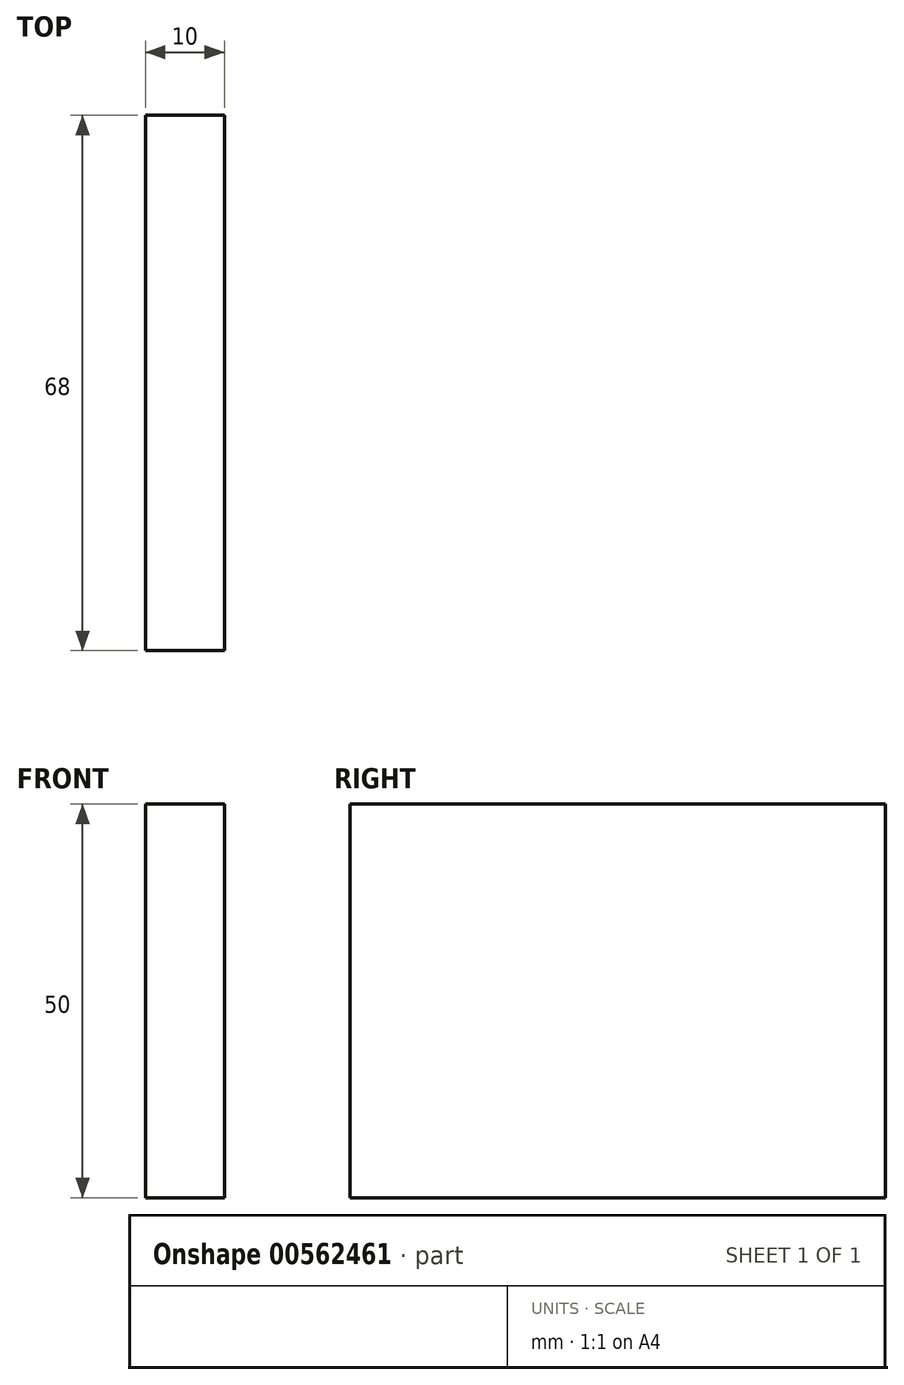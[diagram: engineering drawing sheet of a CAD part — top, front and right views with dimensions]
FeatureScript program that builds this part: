
annotation { "Feature Type Name" : "Feature", "Feature Type Description" : "" }
export const myFeature = defineFeature(function(context is Context, id is Id, definition is map)
    precondition{}
    {
        {
            var Q0;
            Q0=qCreatedBy(makeId("Right.planeOp"),FACE);
            var sketch = newSketch(context, id + "F0", { "sketchPlane" : qUnion([Q0])});
            skLineSegment(sketch, "E0.bottom", {"start": v(-34, 25) * mm, "end": v(34, 25) * mm});
            skLineSegment(sketch, "E0.top", {"start": v(-34, -25) * mm, "end": v(34, -25) * mm});
            skLineSegment(sketch, "E0.left", {"start": v(-34, 25) * mm, "end": v(-34, -25) * mm});
            skLineSegment(sketch, "E0.right", {"start": v(34, 25) * mm, "end": v(34, -25) * mm});
            skPoint(sketch, "E0.middle", {"position": v(0, 0) * mm});
            skSolve(sketch);
        }
        {
            var Q0;
            Q0=makeQuery(id+"F0.imprint","IMPRINT",FACE,{"disambiguationData":[TD([[makeQuery(id+"F0.imprint","IMPRINT",EDGE,{"derivedFrom":sQuery(id+"F0.wireOp",EDGE,"E0.bottom")}),-1.0]])]});
            extrude(context, id + "F1", {"entities" : qUnion([Q0]), "depth" : 10 * mm, "offsetDistance" : 25 * mm, "symmetric" : true});
        }
    });
